# Revit family: Fristående Värmelampa Focus LPF
name_source: partatom
category: Lighting Fixtures
units: mm (PartAtom-declared; Revit-internal decimal feet)

## family parameters
Always vertical = Yes
Cut with Voids When Loaded = No
Light Source = No
OmniClass Number = 23.80.70.11
OmniClass Title = Luminaries for Internal Lighting
Part Type = Normal
Room Calculation Point = No
Round Connector Dimension = Use Diameter
Shared = No
Work Plane-Based = No

## types (6) — shared parameters
Fot = Ø 236 x 12 mm
Height = 635 mm
Leg Material = AMA - Black
Skärm = H 218 / Ø 180 mm
Switch Material = AMA - Black
Voltage = 230 V
Wattage = 250 W
zero-valued in all types: Default Elevation

## per-type parameters (varying)
| type | Main Body Material |
| LPF1-CG | AMA - Cement Grey |
| LPF1-S | AMA - Black |
| LPF1-V | AMA - White |
| LPF1-M | AMA - Brass |
| LPF1-K | AMA - Copper |
| LPF1-RF | AMA - Stainless |

note: column(s) folded — value = type name in every type: Artikelnummer

## geometry (parser evidence)
native form markers: Sweep x2
no freeform markers — native parametric forms only
